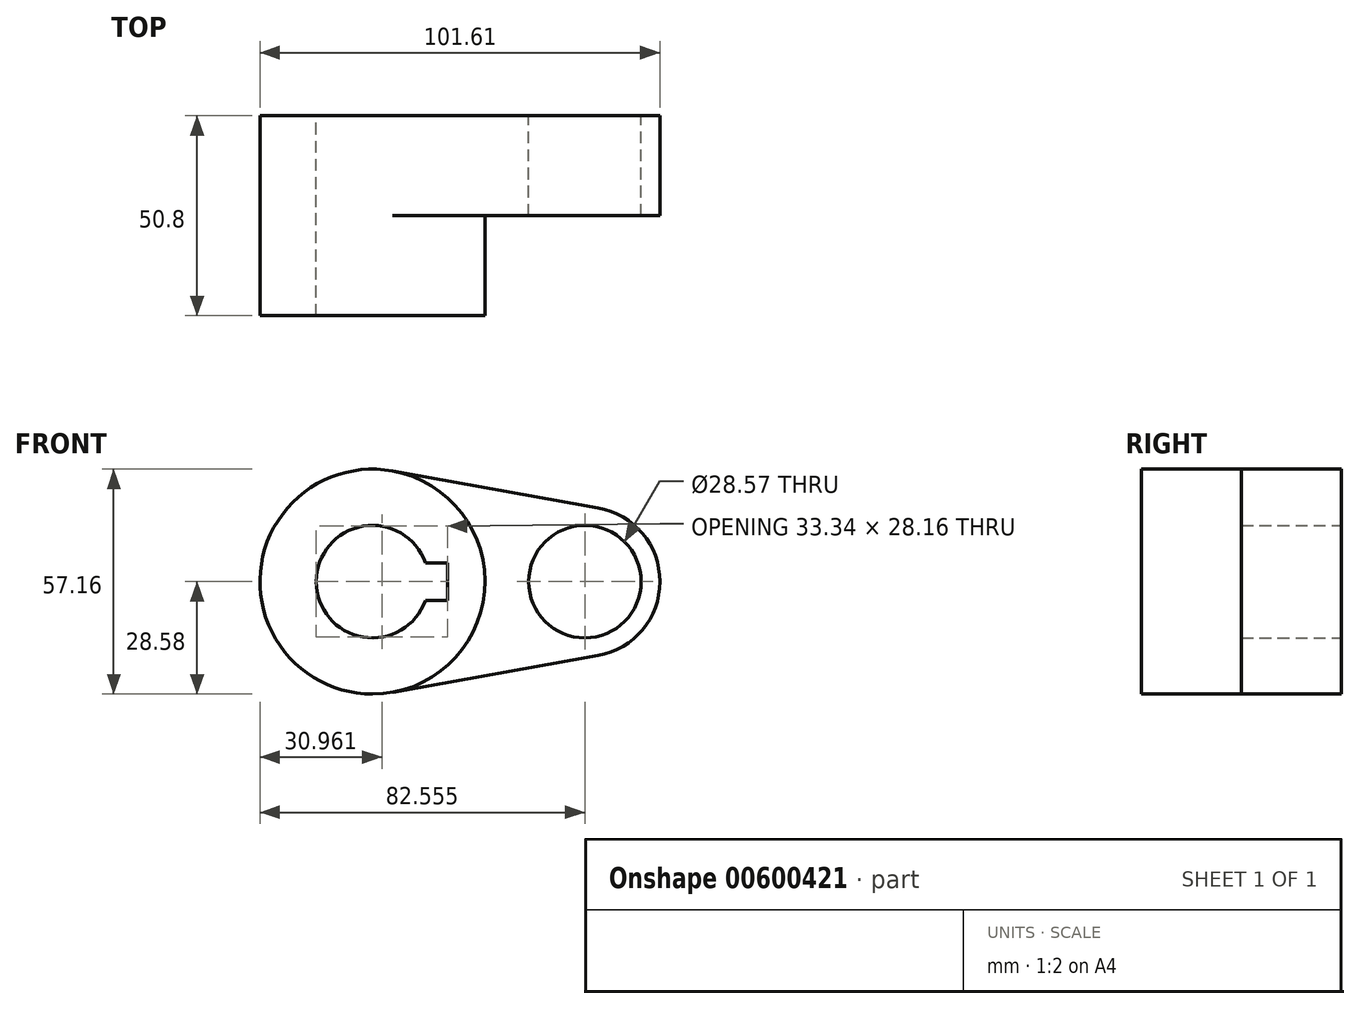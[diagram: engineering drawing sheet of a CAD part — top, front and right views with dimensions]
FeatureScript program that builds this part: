
annotation { "Feature Type Name" : "Feature", "Feature Type Description" : "" }
export const myFeature = defineFeature(function(context is Context, id is Id, definition is map)
    precondition{}
    {
        {
            var Q0;
            Q0=qCreatedBy(makeId("Front.planeOp"),FACE);
            var sketch = newSketch(context, id + "F0", { "sketchPlane" : qUnion([Q0])});
            skCircle(sketch, "E0", {"center": v(0, 0) * mm, "radius": 28.58 * mm});
            skCircle(sketch, "E1", {"center": v(53.98, 0) * mm, "radius": 19.05 * mm});
            skLineSegment(sketch, "E2", {"start": v(5.04, 28.13) * mm, "end": v(57.34, 18.75) * mm});
            skLineSegment(sketch, "E3", {"start": v(5.04, -28.13) * mm, "end": v(57.34, -18.75) * mm});
            skCircle(sketch, "E4", {"center": v(0, 0) * mm, "radius": 14.29 * mm});
            skCircle(sketch, "E5", {"center": v(53.98, 0) * mm, "radius": 14.29 * mm});
            skLineSegment(sketch, "E6.bottom", {"start": v(19.05, -4.76) * mm, "end": v(-19.05, -4.76) * mm});
            skLineSegment(sketch, "E6.top", {"start": v(19.05, 4.76) * mm, "end": v(-19.05, 4.76) * mm});
            skLineSegment(sketch, "E6.left", {"start": v(19.05, -4.76) * mm, "end": v(19.05, 4.76) * mm});
            skLineSegment(sketch, "E6.right", {"start": v(-19.05, -4.76) * mm, "end": v(-19.05, 4.76) * mm});
            skSolve(sketch);
        }
        {
            var Q0;
            {var subQ7=sQuery(id+"F0.wireOp",EDGE,"E6.left");Q0=makeQuery(id+"F0.imprint","IMPRINT",FACE,{"disambiguationData":[TD([[makeQuery(id+"F0.imprint","IMPRINT",EDGE,{"derivedFrom":subQ7}),-1.0]])]});}
            var Q1;
            {var subQ0=sQuery(id+"F0.wireOp",EDGE,"E2");Q1=makeQuery(id+"F0.imprint","IMPRINT",FACE,{"disambiguationData":[TD([[makeQuery(id+"F0.imprint","IMPRINT",EDGE,{"derivedFrom":subQ0}),-1.0]])]});}
            var Q2;
            Q2=makeQuery(id+"F0.imprint","IMPRINT",FACE,{"disambiguationData":[TD([[makeQuery(id+"F0.imprint","IMPRINT",EDGE,{"derivedFrom":sQuery(id+"F0.wireOp",EDGE,"E5")}),-1.0]])]});
            extrude(context, id + "F1", {"entities" : qUnion([Q0, Q1, Q2]), "depth" : 25.4 * mm, "offsetDistance" : 25.4 * mm});
        }
        {
            var Q0;
            {var subQ7=sQuery(id+"F0.wireOp",EDGE,"E6.left");Q0=makeQuery(id+"F0.imprint","IMPRINT",FACE,{"disambiguationData":[TD([[makeQuery(id+"F0.imprint","IMPRINT",EDGE,{"derivedFrom":subQ7}),-1.0]])]});}
            var Q1;
            {var subQ5=sQuery(id+"F0.wireOp",EDGE,"E6.right");Q1=makeQuery(id+"F0.imprint","IMPRINT",FACE,{"disambiguationData":[TD([[makeQuery(id+"F0.imprint","IMPRINT",EDGE,{"derivedFrom":subQ5}),-1.0]])]});}
            extrude(context, id + "F2", {"entities" : qUnion([Q0, Q1]), "operationType" : NewBodyOperationType.ADD, "depth" : 50.8 * mm, "offsetDistance" : 25.4 * mm});
        }
    });
